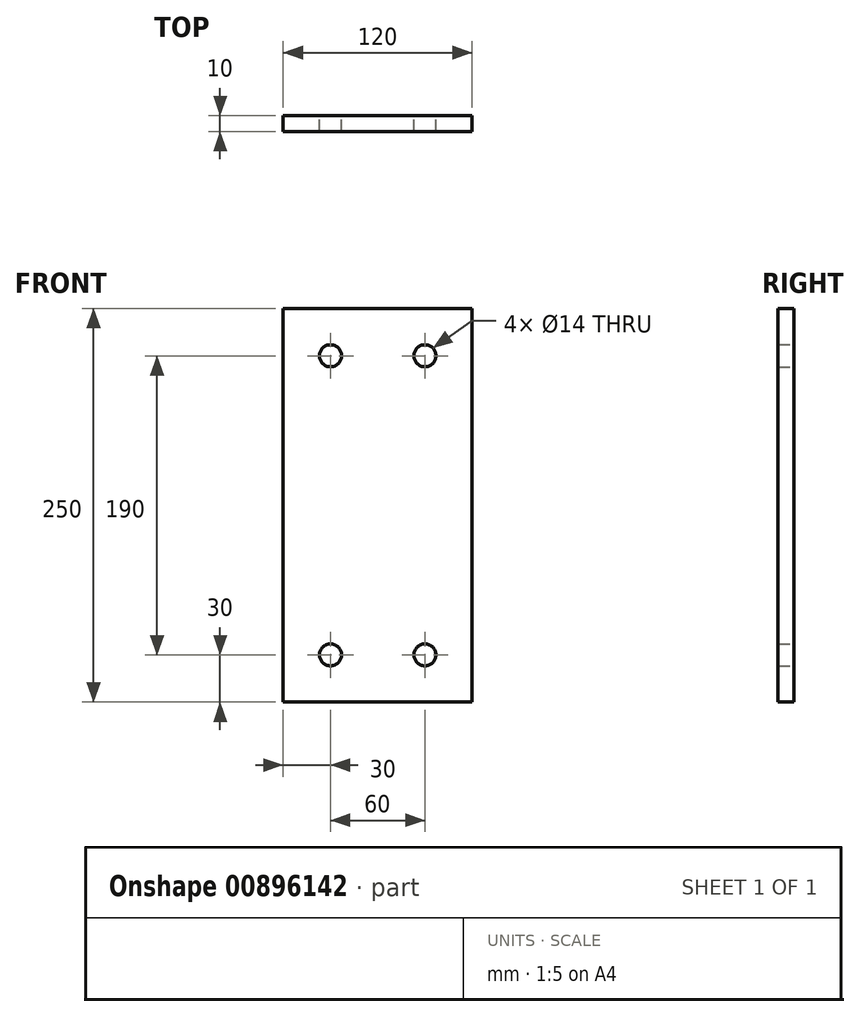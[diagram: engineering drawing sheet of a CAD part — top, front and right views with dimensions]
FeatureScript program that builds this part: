
annotation { "Feature Type Name" : "Feature", "Feature Type Description" : "" }
export const myFeature = defineFeature(function(context is Context, id is Id, definition is map)
    precondition{}
    {
        {
            var Q0;
            Q0=qCreatedBy(makeId("Front.planeOp"),FACE);
            var sketch = newSketch(context, id + "F0", { "sketchPlane" : qUnion([Q0])});
            skLineSegment(sketch, "E0.bottom", {"start": v(60, 125) * mm, "end": v(-60, 125) * mm});
            skLineSegment(sketch, "E0.top", {"start": v(60, -125) * mm, "end": v(-60, -125) * mm});
            skLineSegment(sketch, "E0.left", {"start": v(60, 125) * mm, "end": v(60, -125) * mm});
            skLineSegment(sketch, "E0.right", {"start": v(-60, 125) * mm, "end": v(-60, -125) * mm});
            skPoint(sketch, "E0.middle", {"position": v(0, 0) * mm});
            skCircle(sketch, "E1", {"center": v(-30, 95) * mm, "radius": 7 * mm});
            skCircle(sketch, "E2", {"center": v(30, 95) * mm, "radius": 7 * mm});
            skCircle(sketch, "E3", {"center": v(-30, -95) * mm, "radius": 7 * mm});
            skCircle(sketch, "E4", {"center": v(30, -95) * mm, "radius": 7 * mm});
            skSolve(sketch);
        }
        {
            var Q0;
            Q0=makeQuery(id+"F0.imprint","IMPRINT",FACE,{"disambiguationData":[TD([[makeQuery(id+"F0.imprint","IMPRINT",EDGE,{"derivedFrom":sQuery(id+"F0.wireOp",EDGE,"E0.bottom")}),1.0]])]});
            var Q1;
            Q1=makeQuery(id+"F0.imprint","IMPRINT",FACE,{"disambiguationData":[TD([[makeQuery(id+"F0.imprint","IMPRINT",EDGE,{"derivedFrom":sQuery(id+"F0.wireOp",EDGE,"IxA8HR9I-vB6L-gbE1-t8Bs-stX18FFaMMz4.bottom")}),1.0]])]});
            extrude(context, id + "F1", {"entities" : qUnion([Q0, Q1]), "depth" : 10 * mm, "offsetDistance" : 25 * mm});
        }
    });
